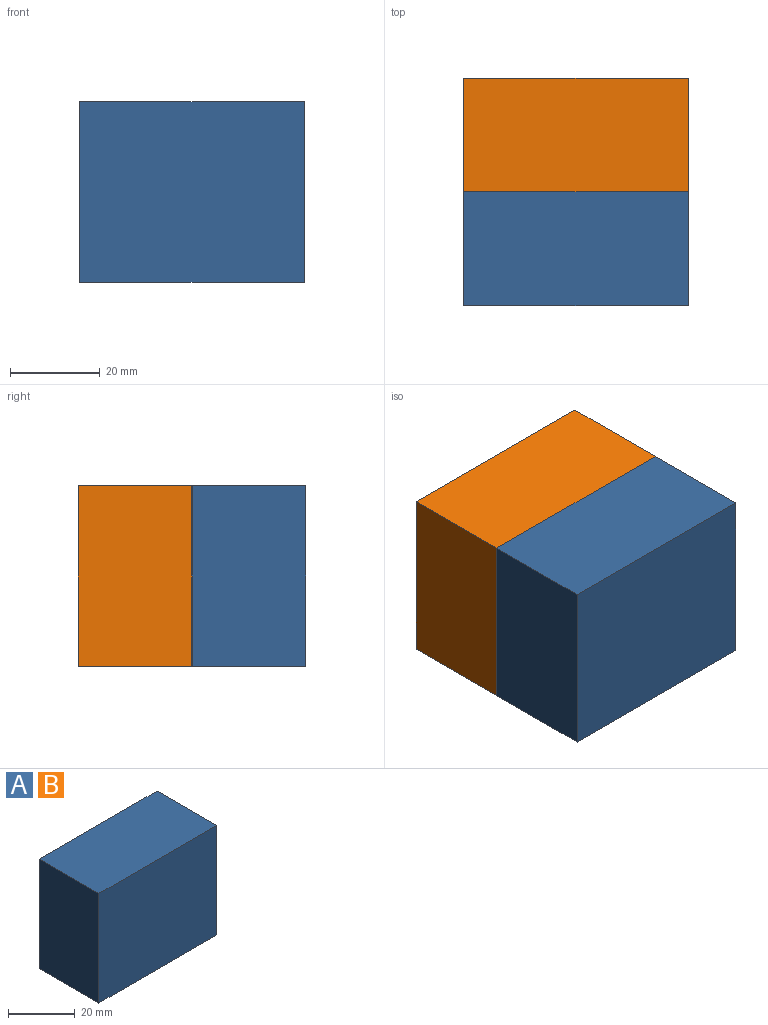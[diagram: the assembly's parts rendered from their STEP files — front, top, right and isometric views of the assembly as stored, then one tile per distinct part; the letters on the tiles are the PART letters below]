
ASSEMBLY  parts=2 mates=1
PART A: 6 faces, bbox 50.1x25.4x40.3 mm
  f0: plane 50.12x25.4mm, normal (0,0,1), area 1273mm2, adj f1,f3,f4,f5
  f1: plane 40.29x25.4mm, normal (-1,0,0), area 1023.3mm2, adj f0,f2,f4,f5
  f2: plane 50.12x25.4mm, normal (0,0,-1), area 1273mm2, adj f1,f3,f4,f5
  f3: plane 40.29x25.4mm, normal (1,0,0), area 1023.3mm2, adj f0,f2,f4,f5
  f4: plane 50.12x40.29mm, normal (0,-1,0), area 2019mm2, adj f0,f1,f2,f3
  f5: plane 50.12x40.29mm, normal (0,1,0), area 2019mm2, adj f0,f1,f2,f3
PART B: same geometry as A
PLACE A rot(axis=(1,0,0),180deg) t=(0,-50.8,35.51)mm
PLACE B at identity
MATE revolute A.f4 <-> B.f4  axis (0,1,0) through (-55.92,-25.4,17.75)mm
